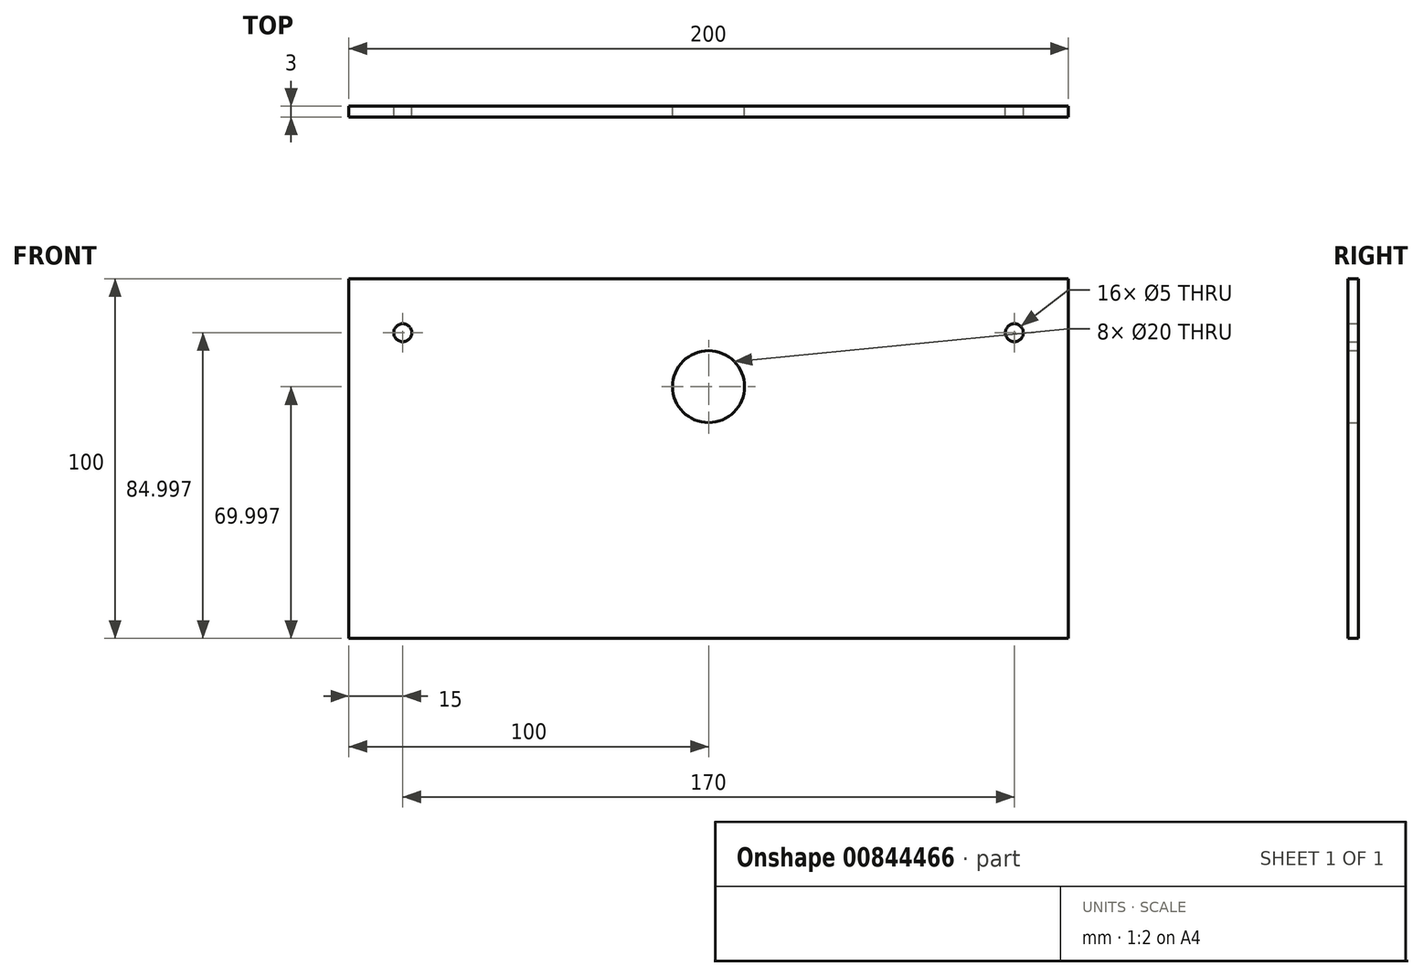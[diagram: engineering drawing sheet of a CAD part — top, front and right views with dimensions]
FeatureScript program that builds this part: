
annotation { "Feature Type Name" : "Feature", "Feature Type Description" : "" }
export const myFeature = defineFeature(function(context is Context, id is Id, definition is map)
    precondition{}
    {
        {
            var Q0;
            Q0=qCreatedBy(makeId("Front.planeOp"),FACE);
            var sketch = newSketch(context, id + "F0", { "sketchPlane" : qUnion([Q0])});
            skLineSegment(sketch, "E0.bottom", {"start": v(-100, 41.39) * mm, "end": v(100, 41.39) * mm});
            skLineSegment(sketch, "E0.top", {"start": v(-100, -58.61) * mm, "end": v(100, -58.61) * mm});
            skLineSegment(sketch, "E0.left", {"start": v(-100, 41.39) * mm, "end": v(-100, -58.61) * mm});
            skLineSegment(sketch, "E0.right", {"start": v(100, 41.39) * mm, "end": v(100, -58.61) * mm});
            skCircle(sketch, "E1", {"center": v(0, 11.39) * mm, "radius": 10 * mm});
            skCircle(sketch, "E2", {"center": v(-85, 26.39) * mm, "radius": 2.5 * mm});
            skCircle(sketch, "E3", {"center": v(85, 26.39) * mm, "radius": 2.5 * mm});
            skSolve(sketch);
        }
        {
            var Q0;
            Q0=makeQuery(id+"F0.imprint","IMPRINT",FACE,{"disambiguationData":[TD([[makeQuery(id+"F0.imprint","IMPRINT",EDGE,{"derivedFrom":sQuery(id+"F0.wireOp",EDGE,"E0.bottom")}),-1.0]])]});
            extrude(context, id + "F1", {"entities" : qUnion([Q0]), "depth" : 3 * mm, "offsetDistance" : 25.4 * mm});
        }
    });
